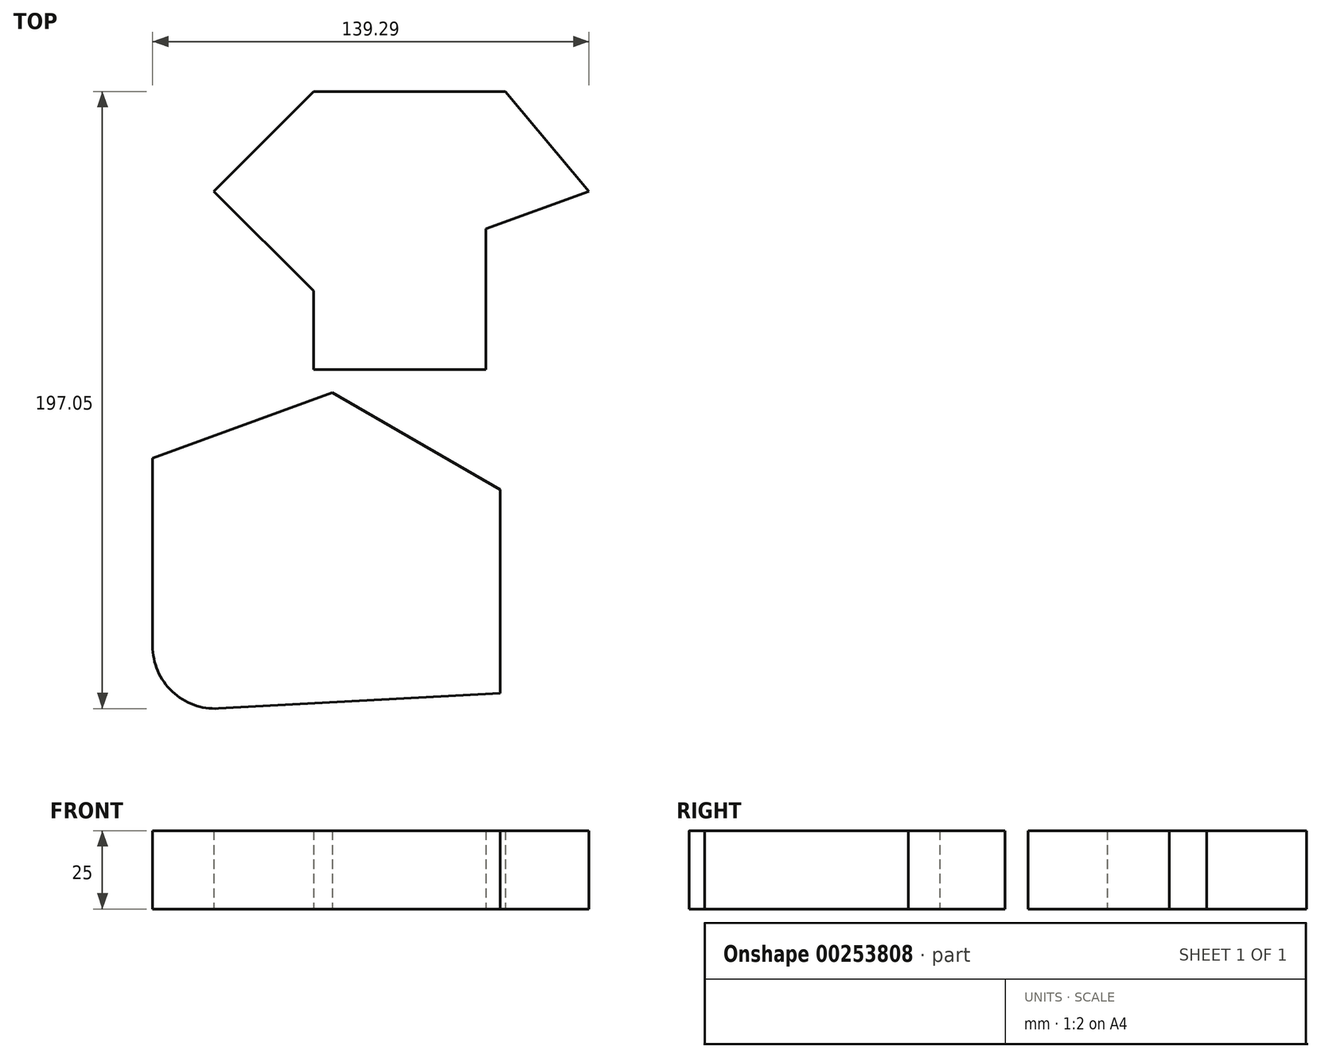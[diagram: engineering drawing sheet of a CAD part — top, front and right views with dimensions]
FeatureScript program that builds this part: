
annotation { "Feature Type Name" : "Feature", "Feature Type Description" : "" }
export const myFeature = defineFeature(function(context is Context, id is Id, definition is map)
    precondition{}
    {
        {
            var Q0;
            Q0=qCreatedBy(makeId("Top.planeOp"),FACE);
            var sketch = newSketch(context, id + "F0", { "sketchPlane" : qUnion([Q0])});
            skLineSegment(sketch, "E0", {"start": v(0, -7.73) * mm, "end": v(55, -7.73) * mm});
            skLineSegment(sketch, "E1", {"start": v(55, -7.73) * mm, "end": v(55, 37.27) * mm});
            skLineSegment(sketch, "E2", {"start": v(55, 37.27) * mm, "end": v(87.89, 49.24) * mm});
            skLineSegment(sketch, "E3", {"start": v(87.89, 49.24) * mm, "end": v(61.19, 81.06) * mm});
            skLineSegment(sketch, "E4", {"start": v(61.19, 81.06) * mm, "end": v(0, 81.06) * mm});
            skLineSegment(sketch, "E5", {"start": v(0, 81.06) * mm, "end": v(-31.82, 49.24) * mm});
            skLineSegment(sketch, "E6", {"start": v(-31.82, 49.24) * mm, "end": v(0, 17.42) * mm});
            skLineSegment(sketch, "E7", {"start": v(0, 17.42) * mm, "end": v(0, -7.73) * mm});
            skLineSegment(sketch, "E8", {"start": v(-51.4, -96) * mm, "end": v(-51.4, -36) * mm});
            skLineSegment(sketch, "E9", {"start": v(-51.4, -36) * mm, "end": v(5.98, -15.1) * mm});
            skLineSegment(sketch, "E10", {"start": v(5.98, -15.1) * mm, "end": v(59.56, -46.04) * mm});
            skLineSegment(sketch, "E11", {"start": v(59.56, -46.04) * mm, "end": v(59.56, -111.04) * mm});
            skLineSegment(sketch, "E12", {"start": v(59.56, -111.04) * mm, "end": v(-30.3, -115.96) * mm});
            skPoint(sketch, "E13.visualSharp", {"position": v(-51.4, -117.12) * mm});
            skArc(sketch, "E13.filletArc", {"start": v(-51.4, -96) * mm, "mid": v(-45.15, -110.51) * mm, "end": v(-30.3, -115.96) * mm});
            skPoint(sketch, "E14.end.orphan", {"position": v(0, -46.04) * mm});
            skSolve(sketch);
        }
        {
            var Q0;
            Q0=makeQuery(id+"F0.imprint","IMPRINT",FACE,{"disambiguationData":[TD([[makeQuery(id+"F0.imprint","IMPRINT",EDGE,{"derivedFrom":sQuery(id+"F0.wireOp",EDGE,"E8")}),-1.0]])]});
            var Q1;
            Q1=makeQuery(id+"F0.imprint","IMPRINT",FACE,{"disambiguationData":[TD([[makeQuery(id+"F0.imprint","IMPRINT",EDGE,{"derivedFrom":sQuery(id+"F0.wireOp",EDGE,"E0")}),1.0]])]});
            extrude(context, id + "F1", {"entities" : qUnion([Q0, Q1]), "depth" : 25 * mm});
        }
    });
